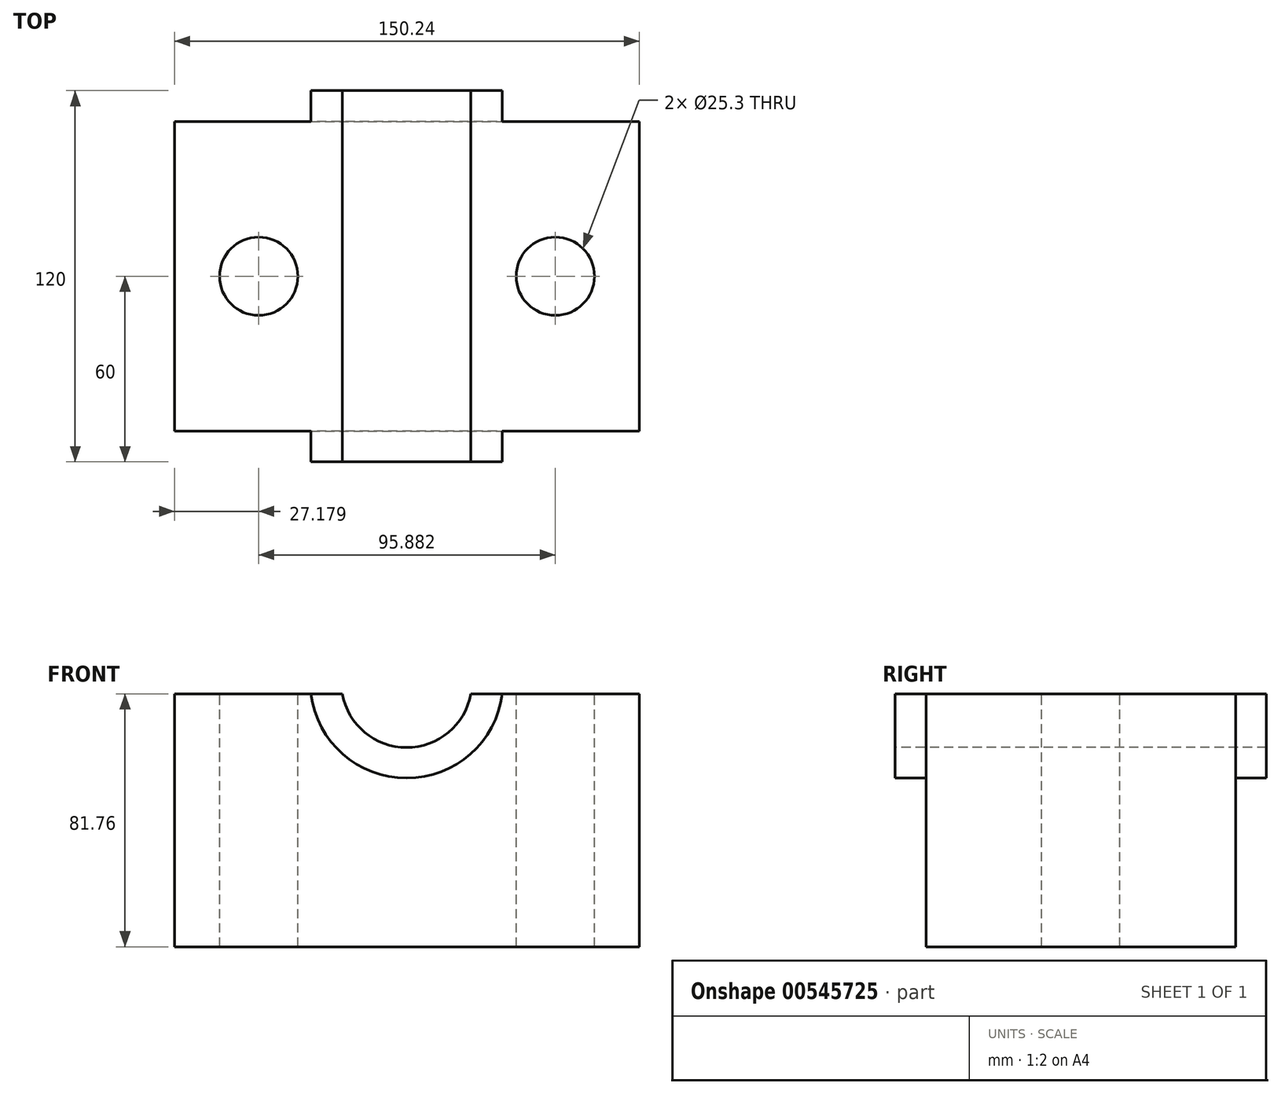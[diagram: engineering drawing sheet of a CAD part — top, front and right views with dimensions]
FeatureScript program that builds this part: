
annotation { "Feature Type Name" : "Feature", "Feature Type Description" : "" }
export const myFeature = defineFeature(function(context is Context, id is Id, definition is map)
    precondition{}
    {
        {
            var Q0;
            Q0=qCreatedBy(makeId("Front.planeOp"),FACE);
            var sketch = newSketch(context, id + "F0", { "sketchPlane" : qUnion([Q0])});
            skLineSegment(sketch, "E0.bottom", {"start": v(75.12, 40.88) * mm, "end": v(-75.12, 40.88) * mm});
            skLineSegment(sketch, "E0.top", {"start": v(75.12, -40.88) * mm, "end": v(-75.12, -40.88) * mm});
            skLineSegment(sketch, "E0.left", {"start": v(75.12, 40.88) * mm, "end": v(75.12, -40.88) * mm});
            skLineSegment(sketch, "E0.right", {"start": v(-75.12, 40.88) * mm, "end": v(-75.12, -40.88) * mm});
            skPoint(sketch, "E0.middle", {"position": v(0, 0) * mm});
            skSolve(sketch);
        }
        {
            var Q0;
            Q0 = qSketchRegion(id + "F0", true);
            extrude(context, id + "F1", {"entities" : qUnion([Q0]), "depth" : 50 * mm, "offsetDistance" : 25 * mm});
        }
        {
            var Q0;
            Q0=makeQuery(id+"F1.opExtrude","CAP_FACE",FACE,{"disambiguationData":[OSD([sQuery(id+"F0.wireOp",EDGE,"E0.bottom"),sQuery(id+"F0.wireOp",EDGE,"E0.top"),sQuery(id+"F0.wireOp",EDGE,"E0.left"),sQuery(id+"F0.wireOp",EDGE,"E0.right")])],"isStart":false});
            var sketch = newSketch(context, id + "F2", { "sketchPlane" : qUnion([Q0])});
            skArc(sketch, "E1", {"start": v(-20.88, 40.88) * mm, "mid": v(-0.13, 23.53) * mm, "end": v(20.63, 40.88) * mm});
            skLineSegment(sketch, "E2", {"start": v(-20.88, 40.88) * mm, "end": v(20.63, 40.88) * mm});
            skSolve(sketch);
        }
        {
            var Q0;
            Q0 = qSketchRegion(id + "F2", true);
            extrude(context, id + "F3", {"entities" : qUnion([Q0]), "operationType" : NewBodyOperationType.REMOVE, "oppositeDirection" : true, "depth" : 166 * mm, "offsetDistance" : 25 * mm});
        }
        {
            var Q0;
            Q0=makeQuery(id+"F1.opExtrude","CAP_FACE",FACE,{"disambiguationData":[OSD([sQuery(id+"F0.wireOp",EDGE,"E0.bottom"),sQuery(id+"F0.wireOp",EDGE,"E0.top"),sQuery(id+"F0.wireOp",EDGE,"E0.left"),sQuery(id+"F0.wireOp",EDGE,"E0.right")])],"isStart":false});
            var sketch = newSketch(context, id + "F4", { "sketchPlane" : qUnion([Q0])});
            skArc(sketch, "E3", {"start": v(-20.88, 40.88) * mm, "mid": v(-0.13, 23.53) * mm, "end": v(20.63, 40.88) * mm});
            skLineSegment(sketch, "E4", {"start": v(-20.88, 40.88) * mm, "end": v(-31.09, 40.88) * mm});
            skLineSegment(sketch, "E5", {"start": v(20.63, 40.88) * mm, "end": v(30.83, 40.88) * mm});
            skArc(sketch, "E6", {"start": v(-31.09, 40.88) * mm, "mid": v(-0.13, 13.64) * mm, "end": v(30.83, 40.88) * mm});
            skSolve(sketch);
        }
        {
            var Q0;
            Q0 = qSketchRegion(id + "F4", true);
            extrude(context, id + "F5", {"entities" : qUnion([Q0]), "operationType" : NewBodyOperationType.ADD, "depth" : 10 * mm, "offsetDistance" : 25 * mm});
        }
        {
            var Q0;
            Q0=makeQuery(id+"F1.opExtrude","SWEPT_BODY",BODY,{"disambiguationData":[OSD([sQuery(id+"F0.wireOp",EDGE,"E0.bottom"),sQuery(id+"F0.wireOp",EDGE,"E0.top"),sQuery(id+"F0.wireOp",EDGE,"E0.left"),sQuery(id+"F0.wireOp",EDGE,"E0.right")])]});
            var Q1;
            Q1=makeQuery(id+"F1.opExtrude","CAP_FACE",FACE,{"disambiguationData":[OSD([sQuery(id+"F0.wireOp",EDGE,"E0.bottom"),sQuery(id+"F0.wireOp",EDGE,"E0.top"),sQuery(id+"F0.wireOp",EDGE,"E0.left"),sQuery(id+"F0.wireOp",EDGE,"E0.right")])],"isStart":true});
            mirror(context, id + "F6", {"operationType" : NewBodyOperationType.ADD, "entities" : qUnion([Q0]), "mirrorPlane" : qUnion([Q1])});
        }
        {
            var Q0;
            {var subQ0=sQuery(id+"F0.wireOp",EDGE,"E0.right");var subQ3=sQuery(id+"F0.wireOp",EDGE,"E0.bottom");var subQ4=makeQuery(id+"F5.boolean.opBoolean","MERGE",FACE,{"derivedFrom":[makeQuery(id+"F3.boolean.opBoolean","SPLIT",FACE,{"disambiguationData":[TD([makeQuery(id+"F1.opExtrude","SWEPT_FACE",FACE,{"disambiguationData":[OSD([subQ0])]})])],"derivedFrom":makeQuery(id+"F1.opExtrude","SWEPT_FACE",FACE,{"disambiguationData":[OSD([subQ3])]})}),makeQuery(id+"F5.opExtrude","SWEPT_FACE",FACE,{"disambiguationData":[OSD([sQuery(id+"F4.wireOp",EDGE,"E4")])]})]});Q0=makeQuery(id+"F6.boolean.opBoolean","MERGE",FACE,{"derivedFrom":[subQ4,makeQuery(id+"F6.opPattern","COPY",FACE,{"derivedFrom":subQ4,"instanceName":"1"})]});}
            var sketch = newSketch(context, id + "F7", { "sketchPlane" : qUnion([Q0])});
            skCircle(sketch, "E7", {"center": v(-47.94, 0) * mm, "radius": 12.65 * mm});
            skCircle(sketch, "E8", {"center": v(47.94, 0) * mm, "radius": 12.65 * mm});
            skSolve(sketch);
        }
        {
            var Q0;
            Q0 = qSketchRegion(id + "F7", true);
            extrude(context, id + "F8", {"entities" : qUnion([Q0]), "operationType" : NewBodyOperationType.REMOVE, "oppositeDirection" : true, "depth" : 89.9 * mm, "offsetDistance" : 25 * mm});
        }
    });
